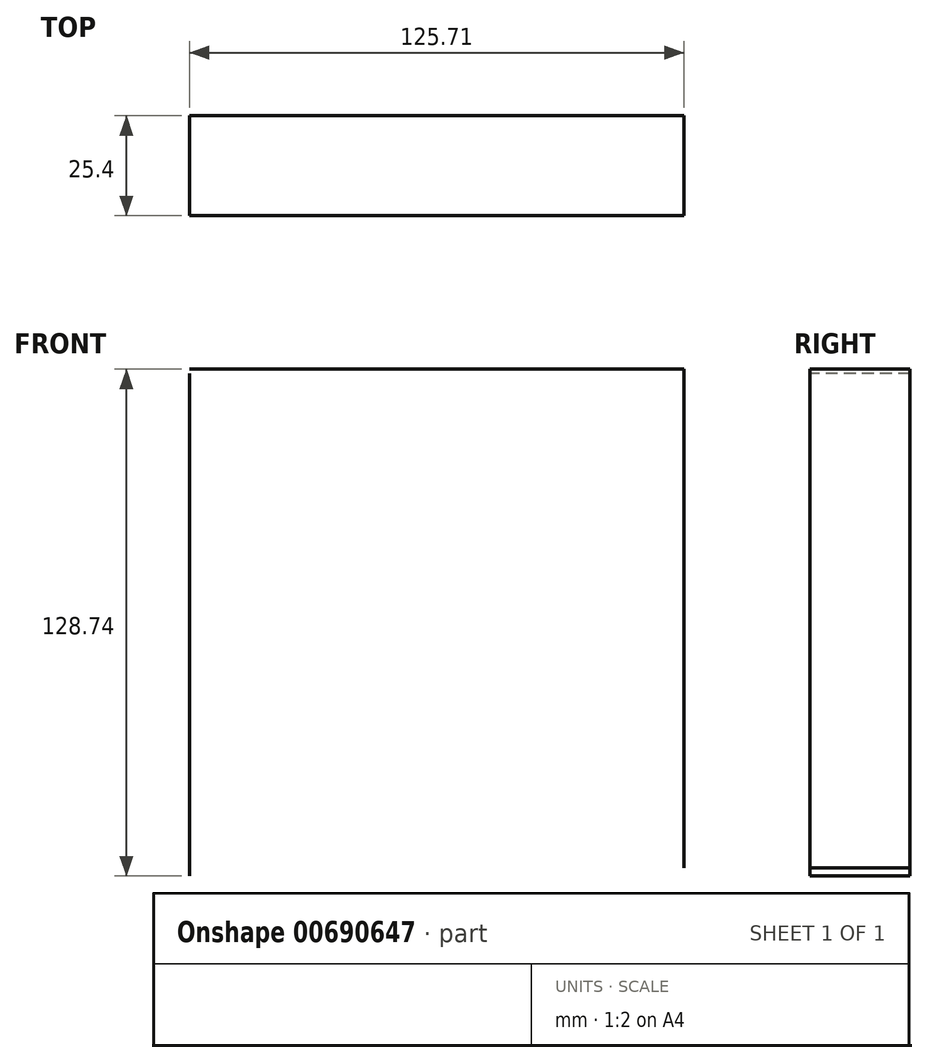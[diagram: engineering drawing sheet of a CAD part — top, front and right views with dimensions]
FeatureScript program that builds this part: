
annotation { "Feature Type Name" : "Feature", "Feature Type Description" : "" }
export const myFeature = defineFeature(function(context is Context, id is Id, definition is map)
    precondition{}
    {
        {
            var Q0;
            Q0=qCreatedBy(makeId("Front.planeOp"),FACE);
            var sketch = newSketch(context, id + "F0", { "sketchPlane" : qUnion([Q0])});
            skLineSegment(sketch, "E0", {"start": v(-76.31, 75.85) * mm, "end": v(-76.31, -76.1) * mm});
            skLineSegment(sketch, "E1", {"start": v(-76.31, -76.1) * mm, "end": v(76.77, -76.1) * mm});
            skLineSegment(sketch, "E2", {"start": v(76.77, -76.1) * mm, "end": v(76.77, 78.3) * mm});
            skLineSegment(sketch, "E3", {"start": v(76.77, 78.3) * mm, "end": v(-76.31, 75.85) * mm});
            skLineSegment(sketch, "E4", {"start": v(-64.71, 62.17) * mm, "end": v(-64.71, -65.45) * mm});
            skLineSegment(sketch, "E5", {"start": v(-64.71, -65.45) * mm, "end": v(61, -63.45) * mm});
            skLineSegment(sketch, "E6", {"start": v(61, -63.45) * mm, "end": v(61, 63.3) * mm});
            skLineSegment(sketch, "E7", {"start": v(61, 63.3) * mm, "end": v(-64.71, 63.3) * mm});
            skSolve(sketch);
        }
        {
            var Q0;
            Q0=sQuery(id+"F0.wireOp",EDGE,"E4");
            var Q1;
            Q1=sQuery(id+"F0.wireOp",EDGE,"E7");
            var Q2;
            Q2=sQuery(id+"F0.wireOp",EDGE,"E6");
            extrude(context, id + "F1", {"bodyType" : ToolBodyType.SURFACE, "surfaceEntities" : qUnion([Q0, Q1, Q2]), "depth" : 25.4 * mm, "offsetDistance" : 25.4 * mm});
        }
    });
